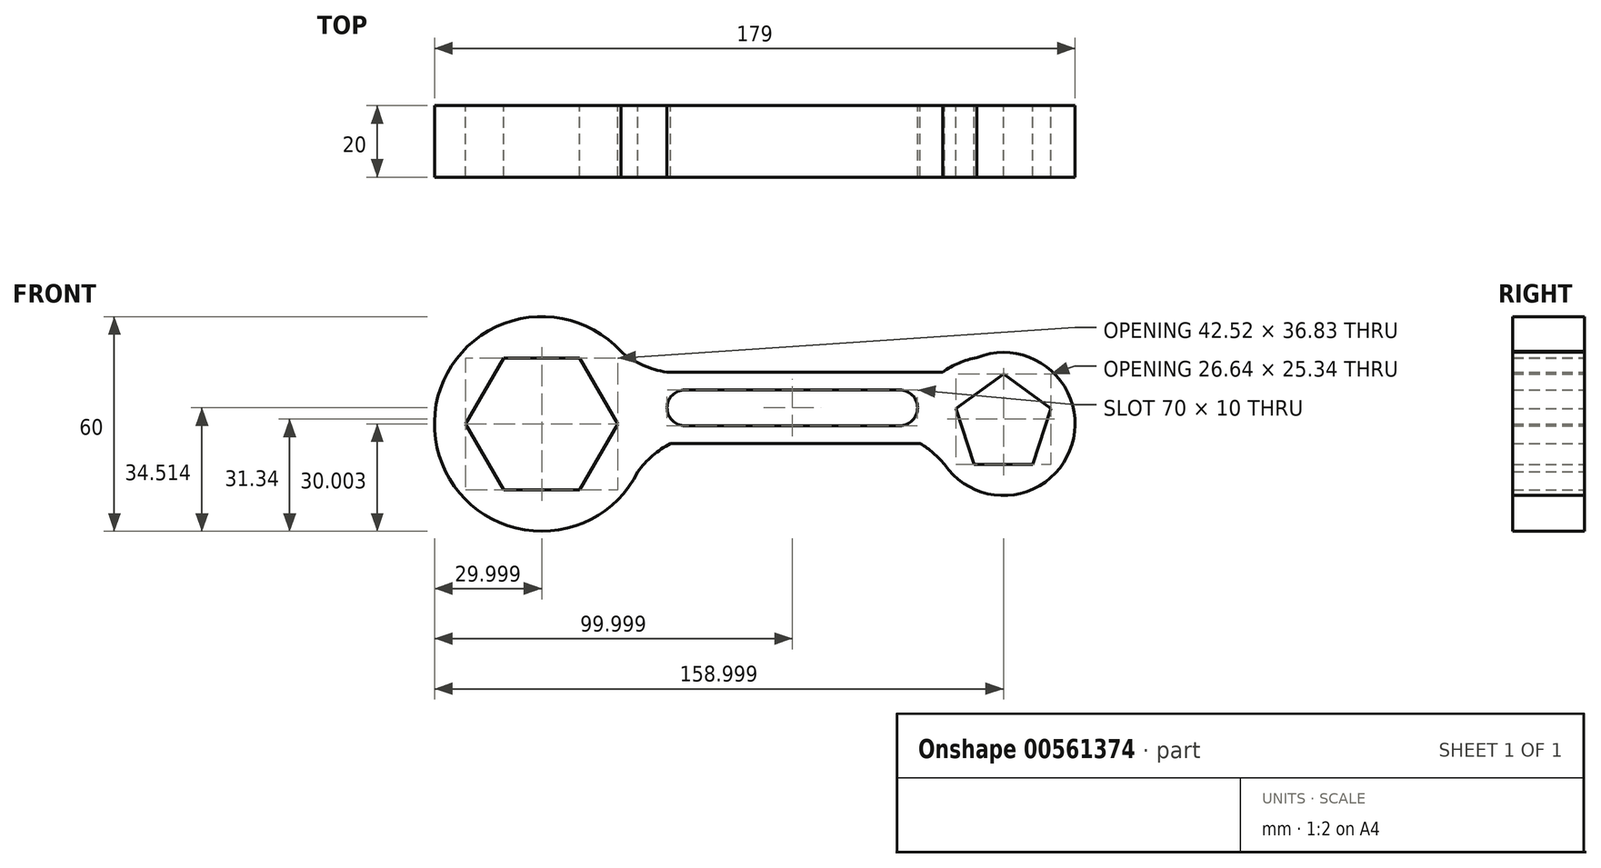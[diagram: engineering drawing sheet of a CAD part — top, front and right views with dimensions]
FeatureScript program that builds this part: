
annotation { "Feature Type Name" : "Feature", "Feature Type Description" : "" }
export const myFeature = defineFeature(function(context is Context, id is Id, definition is map)
    precondition{}
    {
        {
            var Q0;
            Q0=qCreatedBy(makeId("Front.planeOp"),FACE);
            var sketch = newSketch(context, id + "F0", { "sketchPlane" : qUnion([Q0])});
            skCircle(sketch, "E0", {"center": v(-64.45, 18.41) * mm, "radius": 30 * mm});
            skCircle(sketch, "E1", {"center": v(64.55, 18.41) * mm, "radius": 20 * mm});
            skCircle(sketch, "E2.cCircle", {"center": v(-64.45, 18.41) * mm, "radius": 18.41 * mm, "construction": true});
            skLineSegment(sketch, "E2.0", {"start": v(-53.82, 0) * mm, "end": v(-75.08, 0) * mm});
            skLineSegment(sketch, "E2.1", {"start": v(-75.08, 0) * mm, "end": v(-85.71, 18.41) * mm});
            skLineSegment(sketch, "E2.2", {"start": v(-85.71, 18.41) * mm, "end": v(-75.08, 36.83) * mm});
            skLineSegment(sketch, "E2.3", {"start": v(-75.08, 36.83) * mm, "end": v(-53.82, 36.83) * mm});
            skLineSegment(sketch, "E2.4", {"start": v(-53.82, 36.83) * mm, "end": v(-43.19, 18.41) * mm});
            skLineSegment(sketch, "E2.5", {"start": v(-43.19, 18.41) * mm, "end": v(-53.82, 0) * mm});
            skPoint(sketch, "E2.0.midPoint", {"position": v(-64.45, 0) * mm});
            skCircle(sketch, "E3.cCircle", {"center": v(64.55, 18.41) * mm, "radius": 11.33 * mm, "construction": true});
            skLineSegment(sketch, "E3.0", {"start": v(72.78, 7.08) * mm, "end": v(56.32, 7.08) * mm});
            skLineSegment(sketch, "E3.1", {"start": v(56.32, 7.08) * mm, "end": v(51.23, 22.74) * mm});
            skLineSegment(sketch, "E3.2", {"start": v(51.23, 22.74) * mm, "end": v(64.55, 32.42) * mm});
            skLineSegment(sketch, "E3.3", {"start": v(64.55, 32.42) * mm, "end": v(77.87, 22.74) * mm});
            skLineSegment(sketch, "E3.4", {"start": v(77.87, 22.74) * mm, "end": v(72.78, 7.08) * mm});
            skPoint(sketch, "E3.0.midPoint", {"position": v(64.55, 7.08) * mm});
            skLineSegment(sketch, "E4", {"start": v(-38.2, 32.92) * mm, "end": v(50.79, 32.92) * mm});
            skLineSegment(sketch, "E5", {"start": v(-34.96, 12.92) * mm, "end": v(45.32, 12.92) * mm});
            skLineSegment(sketch, "E6.left", {"start": v(-34.45, 18.41) * mm, "end": v(-34.45, 18.41) * mm});
            skLineSegment(sketch, "E6.right", {"start": v(44.55, 18.41) * mm, "end": v(44.55, 18.41) * mm});
            skLineSegment(sketch, "E7.right", {"start": v(-29.45, 18.41) * mm, "end": v(-29.45, 18.41) * mm});
            skLineSegment(sketch, "E8.bottom", {"start": v(-24.45, 27.92) * mm, "end": v(35.55, 27.92) * mm});
            skLineSegment(sketch, "E8.top", {"start": v(-24.45, 17.92) * mm, "end": v(35.55, 17.92) * mm});
            skLineSegment(sketch, "E8.left", {"start": v(-29.45, 22.92) * mm, "end": v(-29.45, 22.92) * mm});
            skLineSegment(sketch, "E8.right", {"start": v(40.55, 22.92) * mm, "end": v(40.55, 22.92) * mm});
            skPoint(sketch, "E9.visualSharp", {"position": v(-29.45, 27.92) * mm});
            skArc(sketch, "E9.filletArc", {"start": v(-24.45, 27.92) * mm, "mid": v(-27.99, 26.46) * mm, "end": v(-29.45, 22.92) * mm});
            skPoint(sketch, "E10.visualSharp", {"position": v(-29.45, 17.92) * mm});
            skArc(sketch, "E10.filletArc", {"start": v(-29.45, 22.92) * mm, "mid": v(-27.99, 19.39) * mm, "end": v(-24.45, 17.92) * mm});
            skPoint(sketch, "E11.visualSharp", {"position": v(40.55, 27.92) * mm});
            skArc(sketch, "E11.filletArc", {"start": v(40.55, 22.92) * mm, "mid": v(39.08, 26.46) * mm, "end": v(35.55, 27.92) * mm});
            skPoint(sketch, "E12.visualSharp", {"position": v(40.55, 17.92) * mm});
            skArc(sketch, "E12.filletArc", {"start": v(35.55, 17.92) * mm, "mid": v(39.08, 19.39) * mm, "end": v(40.55, 22.92) * mm});
            skArc(sketch, "E13", {"start": v(-42.36, 38.71) * mm, "mid": v(-36.32, 34.89) * mm, "end": v(-29.45, 32.92) * mm});
            skArc(sketch, "E14", {"start": v(-28.46, 12.92) * mm, "mid": v(-33.51, 9.54) * mm, "end": v(-37.6, 5.04) * mm});
            skArc(sketch, "E15", {"start": v(57.12, 36.98) * mm, "mid": v(52.11, 35.46) * mm, "end": v(47.53, 32.92) * mm});
            skArc(sketch, "E16", {"start": v(48.07, 7.08) * mm, "mid": v(44.94, 10.3) * mm, "end": v(41.29, 12.92) * mm});
            skSolve(sketch);
        }
        {
            var Q0;
            Q0 = qSketchRegion(id + "F0", true);
            extrude(context, id + "F1", {"entities" : qUnion([Q0]), "depth" : 20 * mm, "offsetDistance" : 25 * mm});
        }
    });
